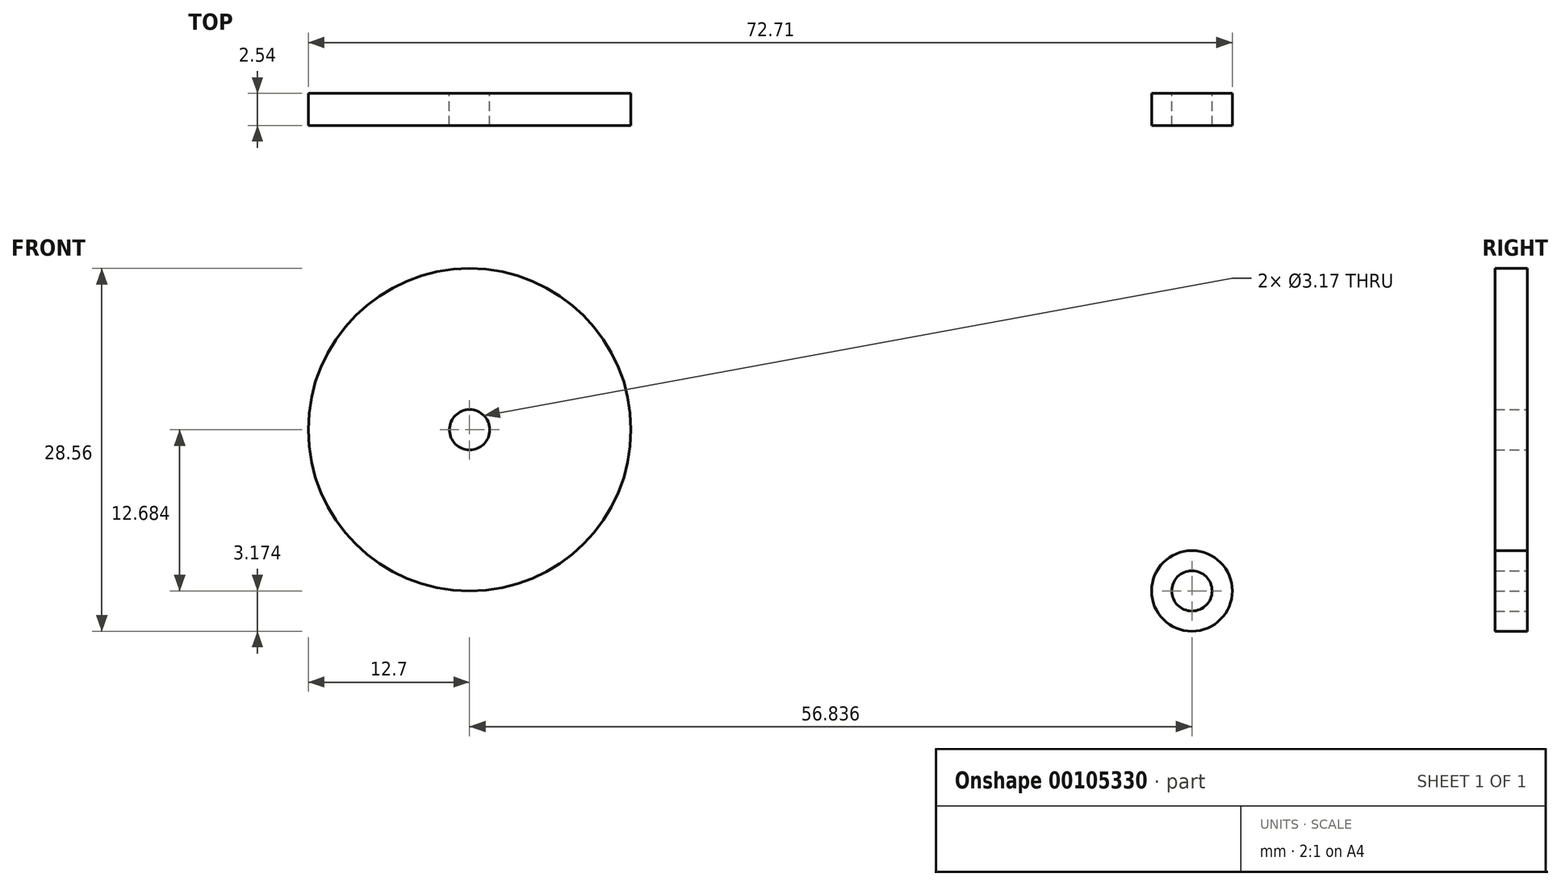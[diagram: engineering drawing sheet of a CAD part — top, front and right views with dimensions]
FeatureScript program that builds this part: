
annotation { "Feature Type Name" : "Feature", "Feature Type Description" : "" }
export const myFeature = defineFeature(function(context is Context, id is Id, definition is map)
    precondition{}
    {
        {
            var Q0;
            Q0=qCreatedBy(makeId("Front.planeOp"),FACE);
            var sketch = newSketch(context, id + "F0", { "sketchPlane" : qUnion([Q0])});
            skCircle(sketch, "E0", {"center": v(-37.8, 35.86) * mm, "radius": 12.7 * mm});
            skCircle(sketch, "E1", {"center": v(19.03, 23.17) * mm, "radius": 3.18 * mm});
            skCircle(sketch, "E2", {"center": v(-37.8, 35.86) * mm, "radius": 1.59 * mm});
            skCircle(sketch, "E3", {"center": v(19.03, 23.17) * mm, "radius": 1.59 * mm});
            skSolve(sketch);
        }
        {
            var Q0;
            Q0=makeQuery(id+"F0.imprint","IMPRINT",FACE,{"disambiguationData":[TD([[makeQuery(id+"F0.imprint","IMPRINT",EDGE,{"derivedFrom":sQuery(id+"F0.wireOp",EDGE,"E0")}),1.0]])]});
            var Q1;
            Q1=makeQuery(id+"F0.imprint","IMPRINT",FACE,{"disambiguationData":[TD([[makeQuery(id+"F0.imprint","IMPRINT",EDGE,{"derivedFrom":sQuery(id+"F0.wireOp",EDGE,"E1")}),1.0]])]});
            extrude(context, id + "F1", {"entities" : qUnion([Q0, Q1]), "depth" : 2.54 * mm});
        }
    });
